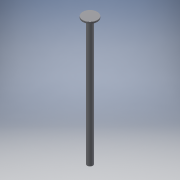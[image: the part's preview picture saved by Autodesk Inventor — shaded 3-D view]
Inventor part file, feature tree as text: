
AUTODESK INVENTOR PART (.ipt)
format: ipt  version: 2016 (Build 200138000, 138)  size: 92,672 bytes
history: native  units: in
note: dims shown in document units (in); Inventor stores cm internally (conversion verified against a paired STEP export)
features: extrude x2, sketch x2
ambient origin geometry x8: Origin, YZ Plane, XZ Plane, XY Plane, X Axis, Y Axis, Z Axis, Center Point
bodies: Solid1 (feature_tree)
feature tree (4):
  extrude  "Extrusion1"  Depth=3.3071in TaperAngle=0.0deg
  extrude  "Extrusion2"  Depth=0.0409in TaperAngle=0.0deg
  sketch  "Sketch1"  dims[d0=0.1496in d1=3.3071in d2=0.0in]
  sketch  "Sketch2"  dims[d3=0.3819in d4=0.0409in d5=0.0in]
